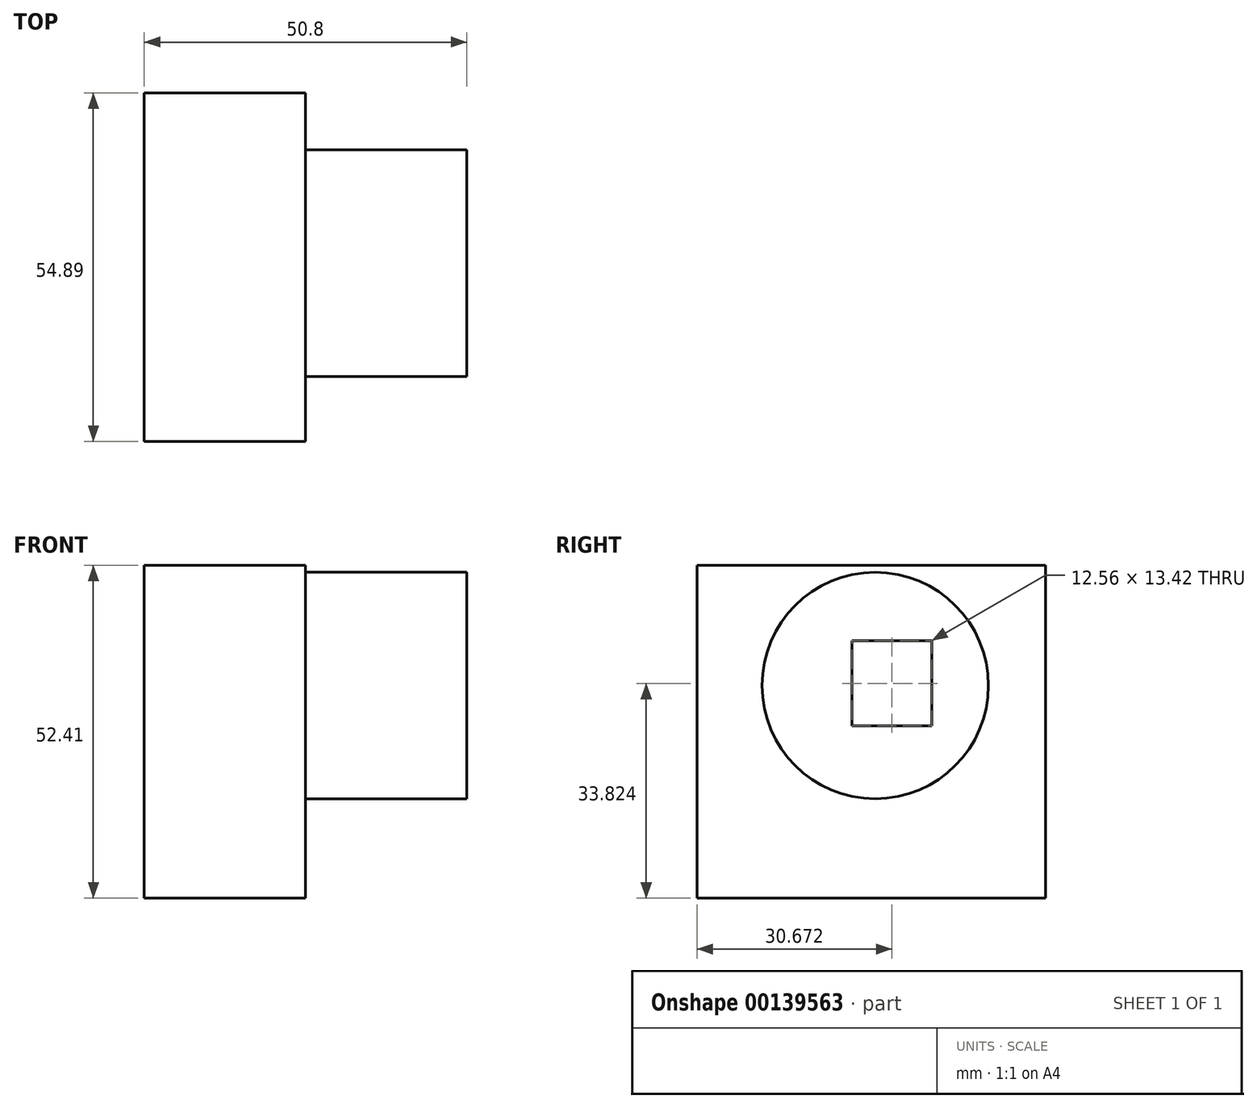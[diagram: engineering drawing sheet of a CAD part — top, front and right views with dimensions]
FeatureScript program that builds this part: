
annotation { "Feature Type Name" : "Feature", "Feature Type Description" : "" }
export const myFeature = defineFeature(function(context is Context, id is Id, definition is map)
    precondition{}
    {
        {
            var Q0;
            Q0=qCreatedBy(makeId("Right.planeOp"),FACE);
            var sketch = newSketch(context, id + "F0", { "sketchPlane" : qUnion([Q0])});
            skLineSegment(sketch, "E0.bottom", {"start": v(0, 0) * mm, "end": v(54.89, 0) * mm});
            skLineSegment(sketch, "E0.top", {"start": v(0, -52.4) * mm, "end": v(54.89, -52.4) * mm});
            skLineSegment(sketch, "E0.left", {"start": v(0, 0) * mm, "end": v(0, -52.4) * mm});
            skLineSegment(sketch, "E0.right", {"start": v(54.89, 0) * mm, "end": v(54.89, -52.4) * mm});
            skSolve(sketch);
        }
        {
            var Q0;
            Q0 = qSketchRegion(id + "F0", true);
            extrude(context, id + "F1", {"entities" : qUnion([Q0]), "depth" : 25.4 * mm});
        }
        {
            var Q0;
            Q0=makeQuery(id+"F1.opExtrude","CAP_FACE",FACE,{"disambiguationData":[OSD([sQuery(id+"F0.wireOp",EDGE,"E0.bottom"),sQuery(id+"F0.wireOp",EDGE,"E0.top"),sQuery(id+"F0.wireOp",EDGE,"E0.left"),sQuery(id+"F0.wireOp",EDGE,"E0.right")])],"isStart":false});
            var sketch = newSketch(context, id + "F2", { "sketchPlane" : qUnion([Q0])});
            skCircle(sketch, "E1", {"center": v(28.06, -18.92) * mm, "radius": 17.82 * mm});
            skSolve(sketch);
        }
        {
            var Q0;
            Q0 = qSketchRegion(id + "F2", true);
            extrude(context, id + "F3", {"entities" : qUnion([Q0]), "operationType" : NewBodyOperationType.ADD, "depth" : 25.4 * mm});
        }
        {
            var Q0;
            Q0=makeQuery(id+"F3.opExtrude","CAP_FACE",FACE,{"disambiguationData":[OSD([sQuery(id+"F2.wireOp",EDGE,"E1")])],"isStart":false});
            var sketch = newSketch(context, id + "F4", { "sketchPlane" : qUnion([Q0])});
            skLineSegment(sketch, "E2.bottom", {"start": v(24.4, -11.88) * mm, "end": v(36.95, -11.88) * mm});
            skLineSegment(sketch, "E2.top", {"start": v(24.4, -25.3) * mm, "end": v(36.95, -25.3) * mm});
            skLineSegment(sketch, "E2.left", {"start": v(24.4, -11.88) * mm, "end": v(24.4, -25.3) * mm});
            skLineSegment(sketch, "E2.right", {"start": v(36.95, -11.88) * mm, "end": v(36.95, -25.3) * mm});
            skSolve(sketch);
        }
        {
            var Q0;
            Q0=makeQuery(id+"F4.imprint","IMPRINT",FACE,{"disambiguationData":[TD([[makeQuery(id+"F4.imprint","IMPRINT",EDGE,{"derivedFrom":sQuery(id+"F4.wireOp",EDGE,"E2.bottom")}),-1.0]])]});
            extrude(context, id + "F5", {"entities" : qUnion([Q0]), "operationType" : NewBodyOperationType.REMOVE, "endBound" : BoundingType.THROUGH_ALL, "oppositeDirection" : true, "depth" : 25.4 * mm});
        }
    });
